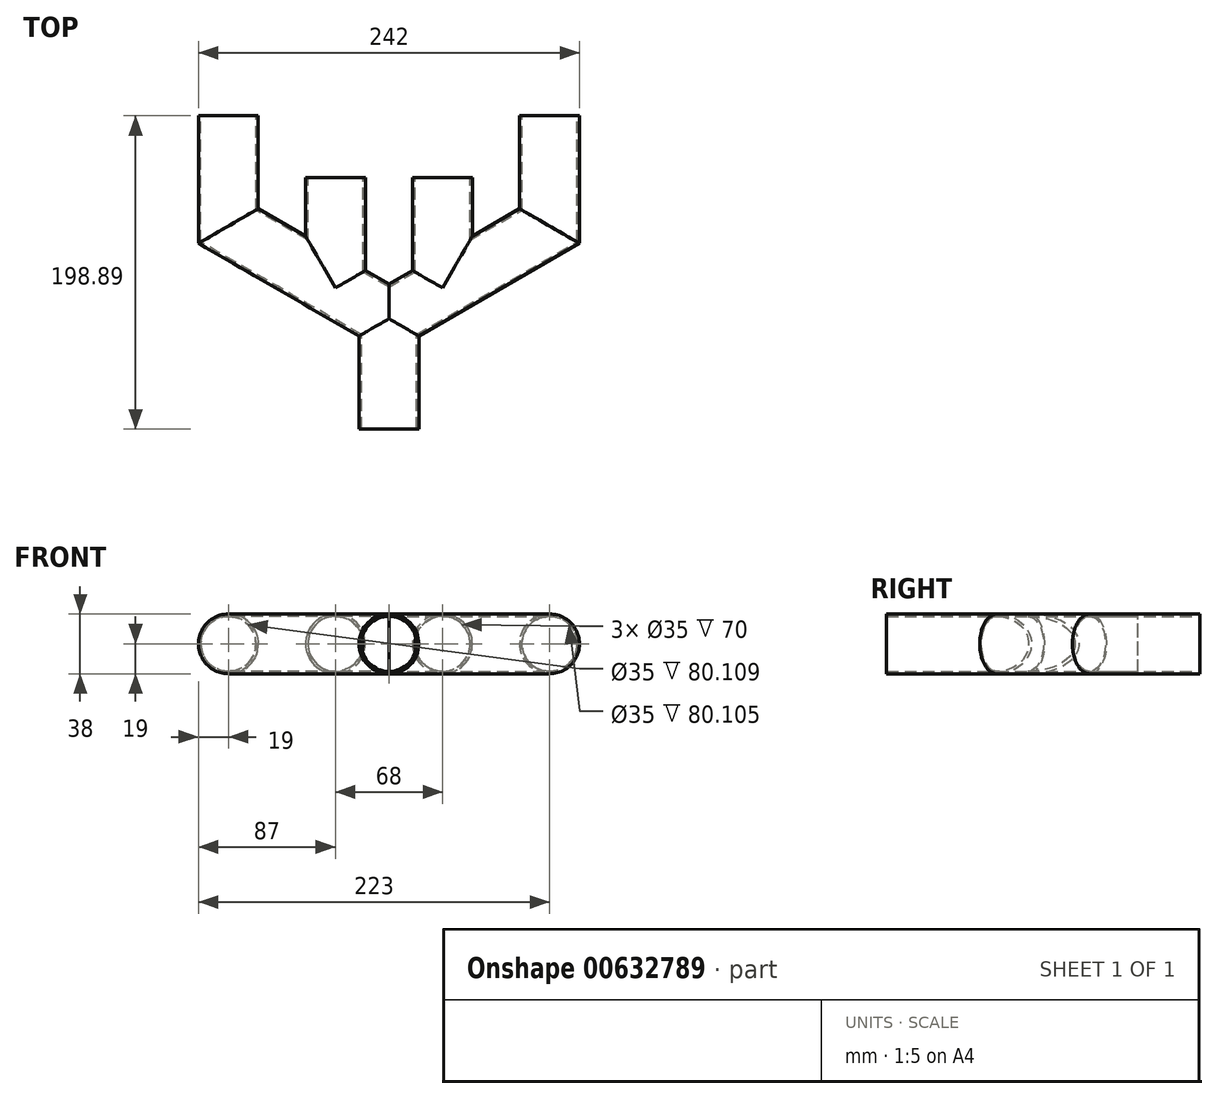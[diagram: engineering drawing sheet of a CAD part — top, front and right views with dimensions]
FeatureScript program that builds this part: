
annotation { "Feature Type Name" : "Feature", "Feature Type Description" : "" }
export const myFeature = defineFeature(function(context is Context, id is Id, definition is map)
    precondition{}
    {
        {
            var Q0;
            Q0=qCreatedBy(makeId("Front.planeOp"),FACE);
            var sketch = newSketch(context, id + "F0", { "sketchPlane" : qUnion([Q0])});
            skCircle(sketch, "E0", {"center": v(0, 0) * mm, "radius": 19 * mm});
            skCircle(sketch, "E1.0", {"center": v(0, 0) * mm, "radius": 17.5 * mm});
            skSolve(sketch);
        }
        {
            var Q0;
            Q0=qCreatedBy(makeId("Top.planeOp"),FACE);
            var sketch = newSketch(context, id + "F1", { "sketchPlane" : qUnion([Q0])});
            skLineSegment(sketch, "E2", {"start": v(0, 0) * mm, "end": v(0, 70) * mm});
            skLineSegment(sketch, "E3", {"start": v(0, 70) * mm, "end": v(-34, 89.63) * mm});
            skLineSegment(sketch, "E4", {"start": v(-34, 89.63) * mm, "end": v(-102, 128.89) * mm});
            skLineSegment(sketch, "E5", {"start": v(-102, 128.89) * mm, "end": v(-83, 128.89) * mm});
            skLineSegment(sketch, "E6", {"start": v(-102, 128.89) * mm, "end": v(-121, 128.89) * mm});
            skLineSegment(sketch, "E7", {"start": v(-102, 128.89) * mm, "end": v(-102, 198.89) * mm});
            skSolve(sketch);
        }
        {
            var Q0;
            Q0=makeQuery(id+"F0.imprint","IMPRINT",FACE,{"disambiguationData":[TD([[makeQuery(id+"F0.imprint","IMPRINT",EDGE,{"derivedFrom":sQuery(id+"F0.wireOp",EDGE,"E0")}),1.0]])]});
            var Q1;
            Q1=sQuery(id+"F1.wireOp",EDGE,"E2");
            var Q2;
            Q2=sQuery(id+"F1.wireOp",EDGE,"E3");
            var Q3;
            Q3=sQuery(id+"F1.wireOp",EDGE,"E4");
            var Q4;
            Q4=sQuery(id+"F1.wireOp",EDGE,"Wua0xxhA-5HR0-JIbY-IgW7-gALE0d99BBlb");
            var Q5;
            Q5=sQuery(id+"F1.wireOp",EDGE,"E7");
            sweep(context, id + "F2", {"profiles" : qUnion([Q0]), "path" : qUnion([Q1, Q2, Q3, Q4, Q5])});
        }
        {
            var Q0;
            Q0=qCreatedBy(makeId("Top.planeOp"),FACE);
            var sketch = newSketch(context, id + "F3", { "sketchPlane" : qUnion([Q0])});
            skLineSegment(sketch, "E8", {"start": v(0, 0) * mm, "end": v(0, 70) * mm});
            skLineSegment(sketch, "E9.MirrorCS", {"start": v(0, 70) * mm, "end": v(34, 89.63) * mm});
            skLineSegment(sketch, "E10.MirrorCS", {"start": v(34, 89.63) * mm, "end": v(102, 128.89) * mm});
            skLineSegment(sketch, "E11.MirrorCS", {"start": v(102, 128.89) * mm, "end": v(83, 128.89) * mm});
            skLineSegment(sketch, "E12.MirrorCS", {"start": v(102, 128.89) * mm, "end": v(121, 128.89) * mm});
            skLineSegment(sketch, "E13.MirrorCS", {"start": v(102, 128.89) * mm, "end": v(102, 198.89) * mm});
            skSolve(sketch);
        }
        {
            var Q0;
            Q0 = qSketchRegion(id + "F0", true);
            var Q1;
            Q1=sQuery(id+"F3.wireOp",EDGE,"E8");
            var Q2;
            Q2=sQuery(id+"F3.wireOp",EDGE,"E9.MirrorCS");
            var Q3;
            Q3=sQuery(id+"F3.wireOp",EDGE,"E10.MirrorCS");
            var Q4;
            Q4=sQuery(id+"F3.wireOp",EDGE,"E13.MirrorCS");
            sweep(context, id + "F4", {"operationType" : NewBodyOperationType.ADD, "profiles" : qUnion([Q0]), "path" : qUnion([Q1, Q2, Q3, Q4])});
        }
        {
            var Q0;
            Q0=qCreatedBy(makeId("Top.planeOp"),FACE);
            var sketch = newSketch(context, id + "F5", { "sketchPlane" : qUnion([Q0])});
            skLineSegment(sketch, "E14", {"start": v(0, 0) * mm, "end": v(0, 70) * mm});
            skLineSegment(sketch, "E15", {"start": v(0, 70) * mm, "end": v(-34, 89.63) * mm});
            skLineSegment(sketch, "E16", {"start": v(-34, 89.63) * mm, "end": v(-34, 159.63) * mm});
            skSolve(sketch);
        }
        {
            var Q0;
            Q0 = qSketchRegion(id + "F0", true);
            var Q1;
            Q1 = qConstructionFilter(qBodyType(qCreatedBy(id + "F0" ,EDGE), BodyType.WIRE), ConstructionObject.NO);
            var Q2;
            Q2=sQuery(id+"F5.wireOp",EDGE,"E14");
            var Q3;
            Q3=sQuery(id+"F5.wireOp",EDGE,"E15");
            var Q4;
            Q4=sQuery(id+"F5.wireOp",EDGE,"E16");
            sweep(context, id + "F6", {"operationType" : NewBodyOperationType.ADD, "profiles" : qUnion([Q0]), "surfaceProfiles" : qUnion([Q1]), "path" : qUnion([Q2, Q3, Q4])});
        }
        {
            var Q0;
            Q0=qCreatedBy(makeId("Top.planeOp"),FACE);
            var sketch = newSketch(context, id + "F7", { "sketchPlane" : qUnion([Q0])});
            skLineSegment(sketch, "E17", {"start": v(0, 0) * mm, "end": v(0, 70) * mm});
            skLineSegment(sketch, "E18.MirrorCS", {"start": v(0, 70) * mm, "end": v(34, 89.63) * mm});
            skLineSegment(sketch, "E19.MirrorCS", {"start": v(34, 89.63) * mm, "end": v(34, 159.63) * mm});
            skSolve(sketch);
        }
        {
            var Q0;
            Q0 = qSketchRegion(id + "F0", true);
            var Q1;
            Q1=sQuery(id+"F7.wireOp",EDGE,"E17");
            var Q2;
            Q2=sQuery(id+"F7.wireOp",EDGE,"E18.MirrorCS");
            var Q3;
            Q3=sQuery(id+"F7.wireOp",EDGE,"E19.MirrorCS");
            sweep(context, id + "F8", {"operationType" : NewBodyOperationType.ADD, "profiles" : qUnion([Q0]), "path" : qUnion([Q1, Q2, Q3])});
        }
        {
            var Q0;
            Q0=makeQuery(id+"F2.opSweep","CAP_FACE",FACE,{"disambiguationData":[OSD([sQuery(id+"F0.wireOp",EDGE,"E0"),sQuery(id+"F0.wireOp",EDGE,"E1.0"),sQuery(id+"F1.wireOp",VERTEX,"E2.start")])],"isStart":true});
            var sketch = newSketch(context, id + "F9", { "sketchPlane" : qUnion([Q0])});
            skCircle(sketch, "E20", {"center": v(0, 0) * mm, "radius": 17.5 * mm});
            skSolve(sketch);
        }
        {
            var Q0;
            Q0 = qSketchRegion(id + "F9", true);
            var Q1;
            Q1=sQuery(id+"F1.wireOp",EDGE,"E2");
            var Q2;
            Q2=sQuery(id+"F1.wireOp",EDGE,"E3");
            var Q3;
            Q3=sQuery(id+"F1.wireOp",EDGE,"E4");
            var Q4;
            Q4=sQuery(id+"F1.wireOp",EDGE,"E7");
            sweep(context, id + "F10", {"operationType" : NewBodyOperationType.REMOVE, "profiles" : qUnion([Q0]), "path" : qUnion([Q1, Q2, Q3, Q4])});
        }
        {
            var Q0;
            Q0 = qSketchRegion(id + "F9", true);
            var Q1;
            Q1=sQuery(id+"F3.wireOp",EDGE,"E8");
            var Q2;
            Q2=sQuery(id+"F3.wireOp",EDGE,"E9.MirrorCS");
            var Q3;
            Q3=sQuery(id+"F3.wireOp",EDGE,"E10.MirrorCS");
            var Q4;
            Q4=sQuery(id+"F3.wireOp",EDGE,"E13.MirrorCS");
            sweep(context, id + "F11", {"operationType" : NewBodyOperationType.REMOVE, "profiles" : qUnion([Q0]), "path" : qUnion([Q1, Q2, Q3, Q4])});
        }
        {
            var Q0;
            Q0 = qSketchRegion(id + "F9", true);
            var Q1;
            Q1=sQuery(id+"F5.wireOp",EDGE,"E14");
            var Q2;
            Q2=sQuery(id+"F5.wireOp",EDGE,"E15");
            var Q3;
            Q3=sQuery(id+"F5.wireOp",EDGE,"E16");
            sweep(context, id + "F12", {"operationType" : NewBodyOperationType.REMOVE, "profiles" : qUnion([Q0]), "path" : qUnion([Q1, Q2, Q3])});
        }
        {
            var Q0;
            Q0 = qSketchRegion(id + "F9", true);
            var Q1;
            Q1=sQuery(id+"F7.wireOp",EDGE,"E17");
            var Q2;
            Q2=sQuery(id+"F7.wireOp",EDGE,"E18.MirrorCS");
            var Q3;
            Q3=sQuery(id+"F7.wireOp",EDGE,"E19.MirrorCS");
            sweep(context, id + "F13", {"operationType" : NewBodyOperationType.REMOVE, "profiles" : qUnion([Q0]), "path" : qUnion([Q1, Q2, Q3])});
        }
    });
